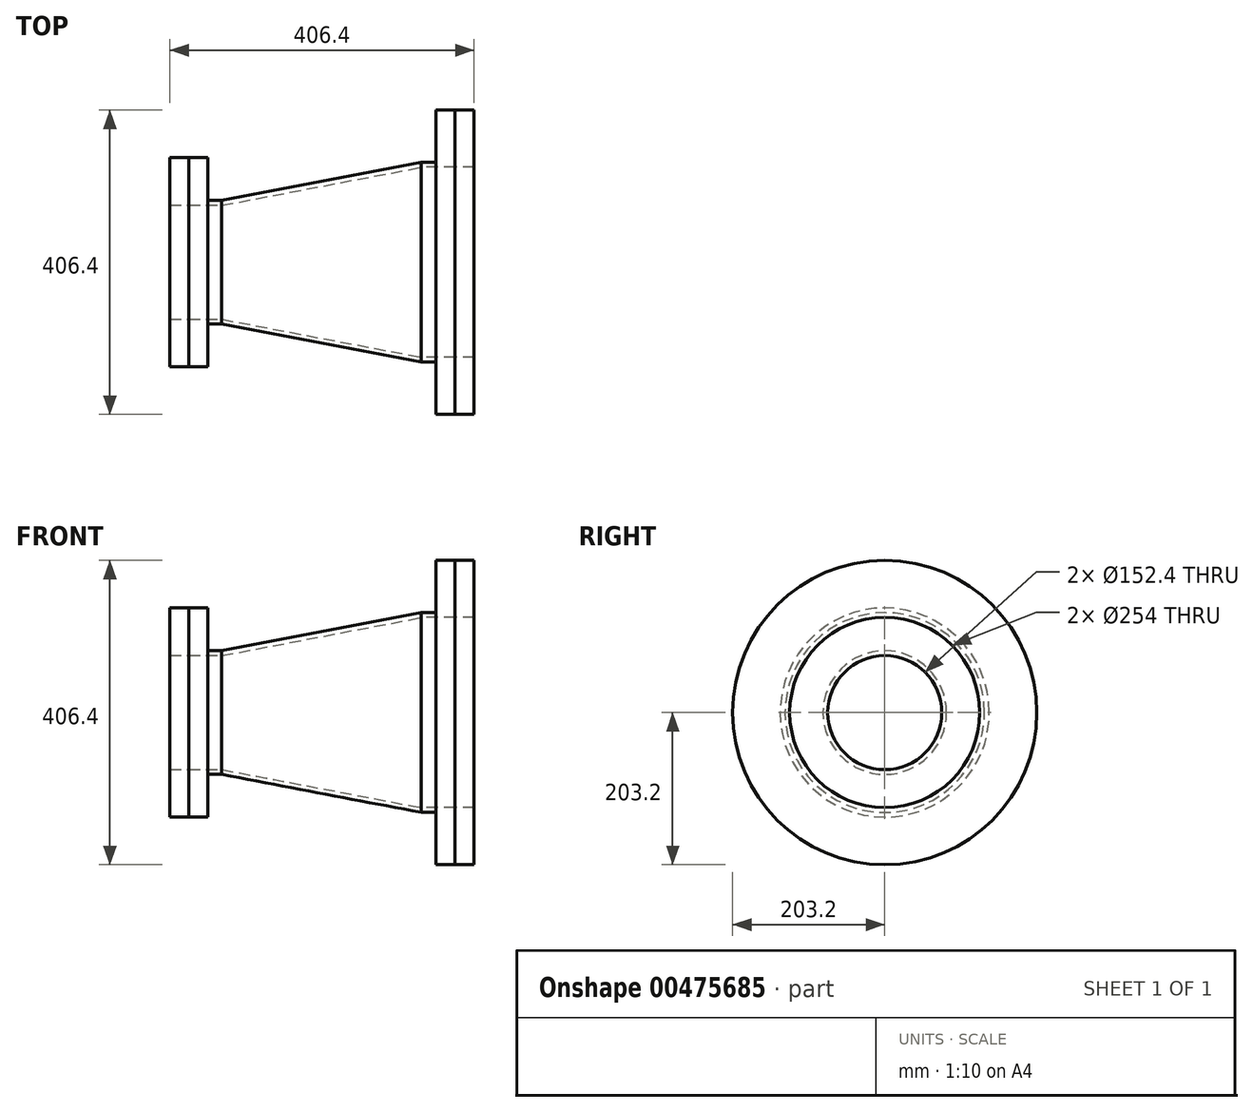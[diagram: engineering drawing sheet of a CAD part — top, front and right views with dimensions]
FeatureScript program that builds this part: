
annotation { "Feature Type Name" : "Feature", "Feature Type Description" : "" }
export const myFeature = defineFeature(function(context is Context, id is Id, definition is map)
    precondition{}
    {
        {
            var Q0;
            Q0=qCreatedBy(makeId("Right.planeOp"),FACE);
            var sketch = newSketch(context, id + "F0", { "sketchPlane" : qUnion([Q0])});
            skCircle(sketch, "E0", {"center": v(0, 0) * mm, "radius": 203.2 * mm});
            skCircle(sketch, "E1", {"center": v(0, 0) * mm, "radius": 127 * mm});
            skSolve(sketch);
        }
        {
            var Q0;
            Q0=makeQuery(id+"F0.imprint","IMPRINT",FACE,{"disambiguationData":[TD([[makeQuery(id+"F0.imprint","IMPRINT",EDGE,{"derivedFrom":sQuery(id+"F0.wireOp",EDGE,"E0")}),1.0]])]});
            extrude(context, id + "F1", {"entities" : qUnion([Q0]), "depth" : 25.4 * mm});
        }
        {
            var Q0;
            Q0=qCreatedBy(makeId("Right.planeOp"),FACE);
            cPlane(context, id + "F2", {"entities" : qUnion([Q0]), "cplaneType" : CPlaneType.OFFSET, "offset" : 304.8 * mm, "oppositeDirection" : true, "width" : 152.4 * mm, "height" : 152.4 * mm});
        }
        {
            var Q0;
            Q0=qCreatedBy(id+"F2.planeOp",FACE);
            var sketch = newSketch(context, id + "F3", { "sketchPlane" : qUnion([Q0])});
            skCircle(sketch, "E2", {"center": v(0, 0) * mm, "radius": 139.7 * mm});
            skCircle(sketch, "E3", {"center": v(0, 0) * mm, "radius": 76.2 * mm});
            skSolve(sketch);
        }
        {
            var Q0;
            Q0=makeQuery(id+"F3.imprint","IMPRINT",FACE,{"disambiguationData":[TD([[makeQuery(id+"F3.imprint","IMPRINT",EDGE,{"derivedFrom":sQuery(id+"F3.wireOp",EDGE,"E2")}),1.0]])]});
            extrude(context, id + "F4", {"entities" : qUnion([Q0]), "oppositeDirection" : true, "depth" : 25.4 * mm});
        }
        {
            var Q0;
            Q0=makeQuery(id+"F1.opExtrude","CAP_FACE",FACE,{"disambiguationData":[OSD([sQuery(id+"F0.wireOp",EDGE,"E0"),sQuery(id+"F0.wireOp",EDGE,"E1")])],"isStart":true});
            var sketch = newSketch(context, id + "F5", { "sketchPlane" : qUnion([Q0])});
            skPoint(sketch, "E4", {"position": v(0, 127) * mm});
            skSolve(sketch);
        }
        {
            var Q0;
            Q0=makeQuery(id+"F4.opExtrude","CAP_FACE",FACE,{"disambiguationData":[OSD([sQuery(id+"F3.wireOp",EDGE,"E2"),sQuery(id+"F3.wireOp",EDGE,"E3")])],"isStart":true});
            var sketch = newSketch(context, id + "F6", { "sketchPlane" : qUnion([Q0])});
            skPoint(sketch, "E5", {"position": v(0, 76.2) * mm});
            skSolve(sketch);
        }
        {
            var Q0;
            Q0=qCreatedBy(makeId("Front.planeOp"),FACE);
            var sketch = newSketch(context, id + "F7", { "sketchPlane" : qUnion([Q0])});
            skLineSegment(sketch, "E6", {"start": v(-304.8, 76.2) * mm, "end": v(-285.75, 76.2) * mm});
            skLineSegment(sketch, "E7", {"start": v(-285.75, 76.2) * mm, "end": v(-19.05, 127) * mm});
            skLineSegment(sketch, "E8", {"start": v(-19.05, 127) * mm, "end": v(0, 127) * mm});
            skLineSegment(sketch, "E9.0", {"start": v(-19.65, 133.35) * mm, "end": v(0, 133.35) * mm});
            skLineSegment(sketch, "E10.0", {"start": v(-286.35, 82.55) * mm, "end": v(-19.65, 133.35) * mm});
            skLineSegment(sketch, "E11.0", {"start": v(-304.8, 82.55) * mm, "end": v(-286.35, 82.55) * mm});
            skLineSegment(sketch, "E12.filletArc", {"start": v(-286.35, 82.55) * mm, "end": v(-286.35, 82.55) * mm});
            skLineSegment(sketch, "E13.filletArc", {"start": v(-19.65, 133.35) * mm, "end": v(-19.65, 133.35) * mm});
            skLineSegment(sketch, "E14", {"start": v(0, 133.35) * mm, "end": v(0, 127) * mm});
            skLineSegment(sketch, "E15", {"start": v(-304.8, 82.55) * mm, "end": v(-304.8, 76.2) * mm});
            skLineSegment(sketch, "E16", {"start": v(0, 0) * mm, "end": v(-300.4, 0) * mm, "construction": true});
            skSolve(sketch);
        }
        {
            var Q0;
            Q0=makeQuery(id+"F7.imprint","IMPRINT",FACE,{"disambiguationData":[TD([[makeQuery(id+"F7.imprint","IMPRINT",EDGE,{"derivedFrom":sQuery(id+"F7.wireOp",EDGE,"E6")}),1.0]])]});
            var Q1;
            Q1=sQuery(id+"F7.wireOp",EDGE,"E16");
            revolve(context, id + "F8", {"operationType" : NewBodyOperationType.ADD, "entities" : qUnion([Q0]), "axis" : qUnion([Q1]), "revolveType" : RevolveType.FULL});
        }
        {
            var Q0;
            Q0=makeQuery(id+"F4.opExtrude","CAP_FACE",FACE,{"disambiguationData":[OSD([sQuery(id+"F3.wireOp",EDGE,"E2"),sQuery(id+"F3.wireOp",EDGE,"E3")])],"isStart":false});
            extrude(context, id + "F9", {"entities" : qUnion([Q0]), "depth" : 25.4 * mm});
        }
        {
            var Q0;
            Q0=makeQuery(id+"F1.opExtrude","CAP_FACE",FACE,{"disambiguationData":[OSD([sQuery(id+"F0.wireOp",EDGE,"E0"),sQuery(id+"F0.wireOp",EDGE,"E1")])],"isStart":false});
            extrude(context, id + "F10", {"entities" : qUnion([Q0]), "depth" : 25.4 * mm});
        }
    });
